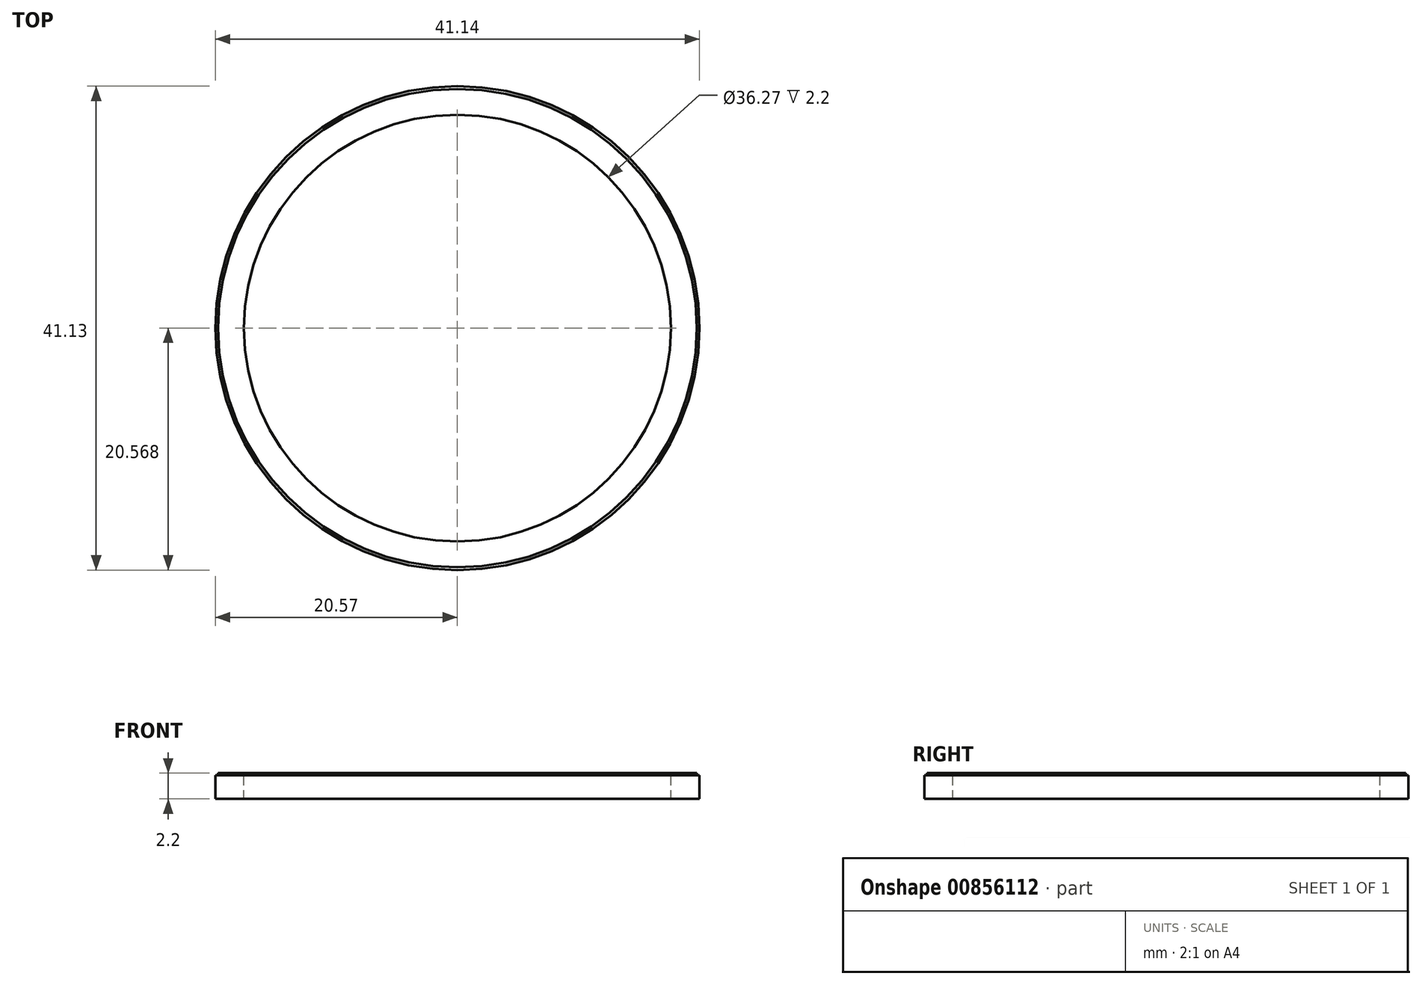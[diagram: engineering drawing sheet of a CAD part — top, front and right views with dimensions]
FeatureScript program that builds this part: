
annotation { "Feature Type Name" : "Feature", "Feature Type Description" : "" }
export const myFeature = defineFeature(function(context is Context, id is Id, definition is map)
    precondition{}
    {
        {
            var Q0;
            Q0=qCreatedBy(makeId("Top.planeOp"),FACE);
            var sketch = newSketch(context, id + "F0", { "sketchPlane" : qUnion([Q0])});
            skCircle(sketch, "E0", {"center": v(0, -0.95) * mm, "radius": 20.57 * mm});
            skCircle(sketch, "E1.0", {"center": v(0, -0.95) * mm, "radius": 18.14 * mm});
            skSolve(sketch);
        }
        {
            var Q0;
            Q0=makeQuery(id+"F0.imprint","IMPRINT",FACE,{"disambiguationData":[TD([[makeQuery(id+"F0.imprint","IMPRINT",EDGE,{"derivedFrom":sQuery(id+"F0.wireOp",EDGE,"E0")}),1.0]])]});
            extrude(context, id + "F1", {"entities" : qUnion([Q0]), "depth" : -2 * mm, "offsetDistance" : 25 * mm});
        }
        {
            var Q0;
            Q0=makeQuery(id+"F1.opExtrude","CAP_FACE",FACE,{"disambiguationData":[OSD([sQuery(id+"F0.wireOp",EDGE,"E0"),sQuery(id+"F0.wireOp",EDGE,"E1.0")])],"isStart":true});
            var sketch = newSketch(context, id + "F2", { "sketchPlane" : qUnion([Q0])});
            skCircle(sketch, "E2.0", {"center": v(0, -0.95) * mm, "radius": 20.33 * mm});
            skSolve(sketch);
        }
        {
            var Q0;
            Q0=makeQuery(id+"F2.imprint","IMPRINT",FACE,{"disambiguationData":[TD([[makeQuery(id+"F2.imprint","IMPRINT",EDGE,{"derivedFrom":sQuery(id+"F2.wireOp",EDGE,"E2.0")}),1.0]])]});
            extrude(context, id + "F3", {"entities" : qUnion([Q0]), "operationType" : NewBodyOperationType.ADD, "depth" : 0.2 * mm, "offsetDistance" : 25 * mm});
        }
    });
